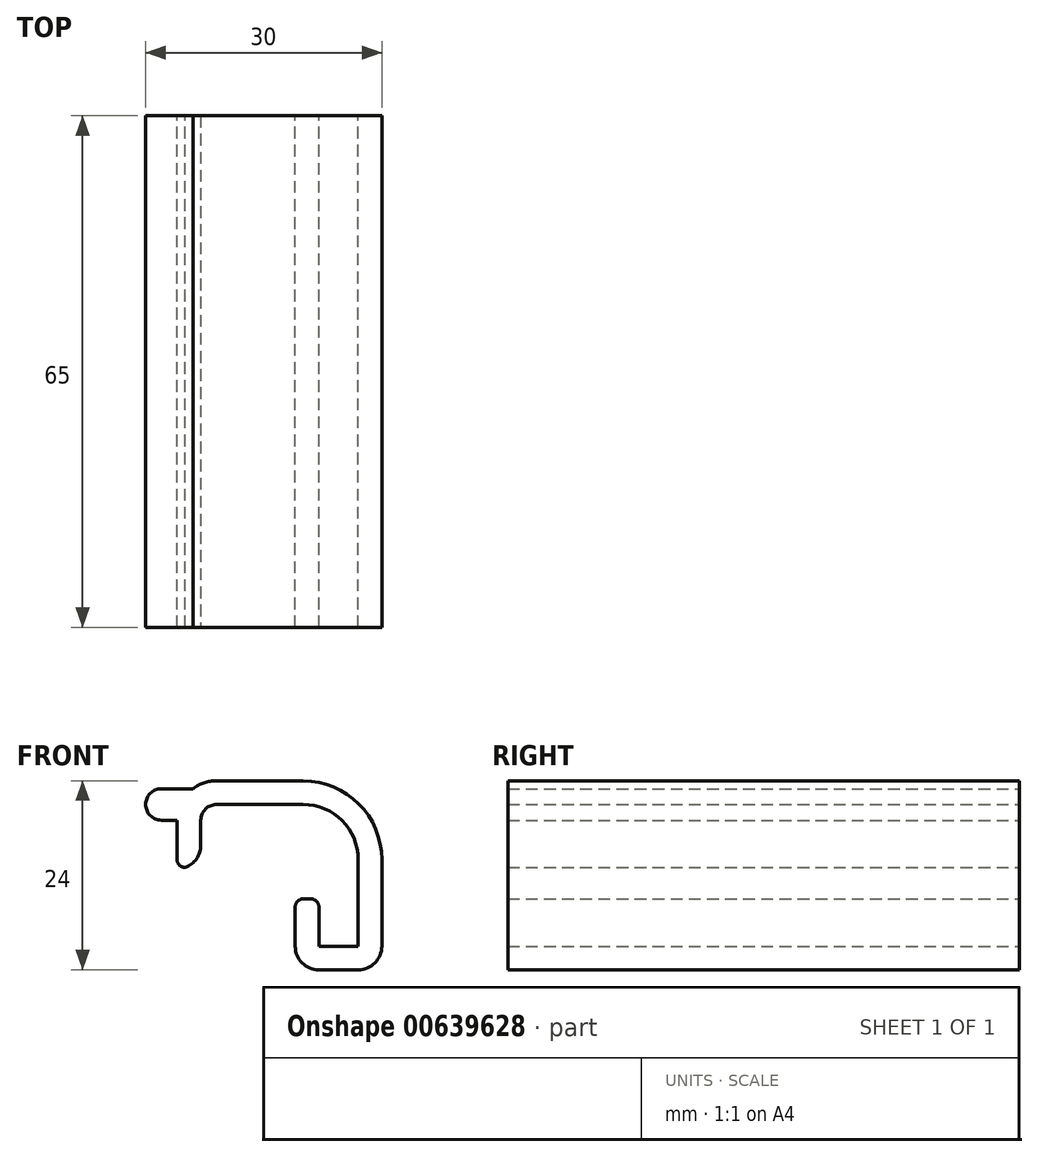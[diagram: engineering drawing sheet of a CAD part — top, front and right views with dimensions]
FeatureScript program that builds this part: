
annotation { "Feature Type Name" : "Feature", "Feature Type Description" : "" }
export const myFeature = defineFeature(function(context is Context, id is Id, definition is map)
    precondition{}
    {
        {
            var Q0;
            Q0=qCreatedBy(makeId("Front.planeOp"),FACE);
            var sketch = newSketch(context, id + "F0", { "sketchPlane" : qUnion([Q0])});
            skLineSegment(sketch, "E0", {"start": v(2, 0) * mm, "end": v(13, 0) * mm});
            skLineSegment(sketch, "E1", {"start": v(20, -7) * mm, "end": v(20, -18) * mm});
            skLineSegment(sketch, "E2", {"start": v(20, -18) * mm, "end": v(15, -18) * mm});
            skLineSegment(sketch, "E3", {"start": v(15, -18) * mm, "end": v(15, -12) * mm});
            skLineSegment(sketch, "E4", {"start": v(0, -2) * mm, "end": v(0, -8) * mm});
            skPoint(sketch, "E5.visualSharp", {"position": v(20, 0) * mm});
            skArc(sketch, "E5.filletArc", {"start": v(20, -7) * mm, "mid": v(17.95, -2.05) * mm, "end": v(13, 0) * mm});
            skPoint(sketch, "E6.visualSharp", {"position": v(15, -18) * mm});
            skLineSegment(sketch, "E6.filletArc", {"start": v(15, -18) * mm, "end": v(15, -18) * mm});
            skPoint(sketch, "E7.visualSharp", {"position": v(20, -18) * mm});
            skLineSegment(sketch, "E7.filletArc", {"start": v(20, -18) * mm, "end": v(20, -18) * mm});
            skPoint(sketch, "E8.visualSharp", {"position": v(0, 0) * mm});
            skArc(sketch, "E8.filletArc", {"start": v(2, 0) * mm, "mid": v(0.59, -0.59) * mm, "end": v(0, -2) * mm});
            skLineSegment(sketch, "E9.0", {"start": v(-3, -2) * mm, "end": v(-3, -8) * mm});
            skArc(sketch, "E9.1", {"start": v(2, 3) * mm, "mid": v(-1.54, 1.54) * mm, "end": v(-3, -2) * mm});
            skLineSegment(sketch, "E9.2", {"start": v(2, 3) * mm, "end": v(13, 3) * mm});
            skArc(sketch, "E9.3", {"start": v(23, -7) * mm, "mid": v(20.07, 0.07) * mm, "end": v(13, 3) * mm});
            skLineSegment(sketch, "E9.4", {"start": v(23, -7) * mm, "end": v(23, -18) * mm});
            skLineSegment(sketch, "E9.5", {"start": v(12, -18) * mm, "end": v(12, -12) * mm});
            skArc(sketch, "E9.6", {"start": v(12, -18) * mm, "mid": v(12.88, -20.12) * mm, "end": v(15, -21) * mm});
            skLineSegment(sketch, "E9.7", {"start": v(20, -21) * mm, "end": v(15, -21) * mm});
            skArc(sketch, "E9.8", {"start": v(20, -21) * mm, "mid": v(22.12, -20.12) * mm, "end": v(23, -18) * mm});
            skLineSegment(sketch, "E10", {"start": v(-3, -8) * mm, "end": v(0, -8) * mm});
            skLineSegment(sketch, "E11", {"start": v(12, -12) * mm, "end": v(15, -12) * mm});
            skLineSegment(sketch, "E12", {"start": v(-3, -2) * mm, "end": v(-7, -2) * mm});
            skLineSegment(sketch, "E13", {"start": v(-7, -2) * mm, "end": v(-7, 2) * mm});
            skLineSegment(sketch, "E14", {"start": v(-7, 2) * mm, "end": v(-1, 2) * mm});
            skSolve(sketch);
        }
        {
            var Q0;
            Q0=makeQuery(id+"F0.imprint","IMPRINT",FACE,{"disambiguationData":[TD([[makeQuery(id+"F0.imprint","IMPRINT",EDGE,{"derivedFrom":sQuery(id+"F0.wireOp",EDGE,"E0")}),1.0]])]});
            var Q1;
            {var subQ0=sQuery(id+"F0.wireOp",EDGE,"E12");Q1=makeQuery(id+"F0.imprint","IMPRINT",FACE,{"disambiguationData":[TD([[makeQuery(id+"F0.imprint","IMPRINT",EDGE,{"derivedFrom":subQ0}),-1.0]])]});}
            extrude(context, id + "F1", {"entities" : qUnion([Q0, Q1]), "depth" : 65 * mm, "offsetDistance" : 25 * mm});
        }
        {
            var Q0;
            Q0=makeQuery(id+"F1.opExtrude","SWEPT_EDGE",EDGE,{"disambiguationData":[OSD([sQuery(id+"F0.wireOp",EDGE,"eZ8F8BY3-ax1E-NWox-5bNF-6wtKU76AMF4s"),sQuery(id+"F0.wireOp",EDGE,"JfX7uQPt-sGsW-Cpx5-vXd5-tcMYiyzHYluC")])]});
            var Q1;
            Q1=makeQuery(id+"F1.opExtrude","SWEPT_EDGE",EDGE,{"disambiguationData":[OSD([sQuery(id+"F0.wireOp",EDGE,"E9.0"),sQuery(id+"F0.wireOp",EDGE,"E10")])]});
            var Q2;
            Q2=makeQuery(id+"F1.opExtrude","SWEPT_EDGE",EDGE,{"disambiguationData":[OSD([sQuery(id+"F0.wireOp",EDGE,"E9.5"),sQuery(id+"F0.wireOp",EDGE,"E11")])]});
            var Q3;
            Q3=makeQuery(id+"F1.opExtrude","SWEPT_EDGE",EDGE,{"disambiguationData":[OSD([sQuery(id+"F0.wireOp",EDGE,"E3"),sQuery(id+"F0.wireOp",EDGE,"E11")])]});
            fillet(context, id + "F2", {"entities" : qUnion([Q0, Q1, Q2, Q3]), "radius" : 1 * mm, "tangentPropagation" : true, "allowEdgeOverflow" : false});
        }
        {
            var Q0;
            Q0=makeQuery(id+"F1.opExtrude","SWEPT_EDGE",EDGE,{"disambiguationData":[OSD([sQuery(id+"F0.wireOp",EDGE,"E12"),sQuery(id+"F0.wireOp",EDGE,"E13")])]});
            var Q1;
            Q1=makeQuery(id+"F1.opExtrude","SWEPT_EDGE",EDGE,{"disambiguationData":[OSD([sQuery(id+"F0.wireOp",EDGE,"E13"),sQuery(id+"F0.wireOp",EDGE,"E14")])]});
            fillet(context, id + "F3", {"entities" : qUnion([Q0, Q1]), "radius" : 2 * mm, "tangentPropagation" : true, "allowEdgeOverflow" : false});
        }
        {
            var Q0;
            Q0=makeQuery(id+"F1.opExtrude","SWEPT_EDGE",EDGE,{"disambiguationData":[OSD([sQuery(id+"F0.wireOp",EDGE,"E4"),sQuery(id+"F0.wireOp",EDGE,"E10")])]});
            fillet(context, id + "F4", {"entities" : qUnion([Q0]), "radius" : 3 * mm, "tangentPropagation" : true, "allowEdgeOverflow" : false});
        }
    });
